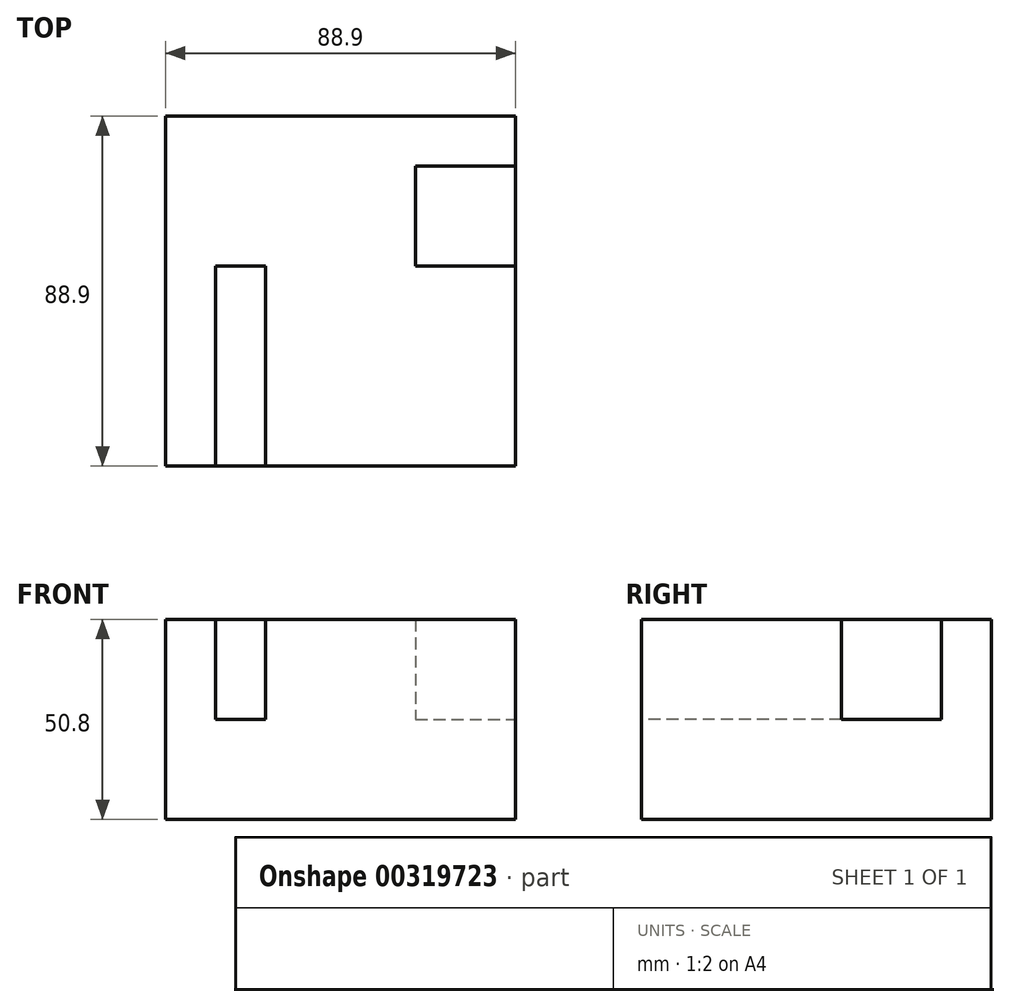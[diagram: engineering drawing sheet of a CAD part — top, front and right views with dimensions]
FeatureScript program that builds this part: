
annotation { "Feature Type Name" : "Feature", "Feature Type Description" : "" }
export const myFeature = defineFeature(function(context is Context, id is Id, definition is map)
    precondition{}
    {
        {
            var Q0;
            Q0=qCreatedBy(makeId("Top.planeOp"),FACE);
            var sketch = newSketch(context, id + "F0", { "sketchPlane" : qUnion([Q0])});
            skLineSegment(sketch, "E0", {"start": v(-35.04, 28.06) * mm, "end": v(-35.04, -60.84) * mm});
            skLineSegment(sketch, "E1", {"start": v(-35.04, -60.84) * mm, "end": v(53.86, -60.84) * mm});
            skLineSegment(sketch, "E2", {"start": v(53.86, -60.84) * mm, "end": v(53.86, 28.06) * mm});
            skLineSegment(sketch, "E3", {"start": v(53.86, 28.06) * mm, "end": v(-35.04, 28.06) * mm});
            skSolve(sketch);
        }
        {
            var Q0;
            Q0=makeQuery(id+"F0.imprint","IMPRINT",FACE,{"disambiguationData":[TD([[makeQuery(id+"F0.imprint","IMPRINT",EDGE,{"derivedFrom":sQuery(id+"F0.wireOp",EDGE,"E0")}),1.0]])]});
            extrude(context, id + "F1", {"entities" : qUnion([Q0]), "depth" : 50.8 * mm});
        }
        {
            var Q0;
            Q0=makeQuery(id+"F1.opExtrude","SWEPT_FACE",FACE,{"disambiguationData":[OSD([sQuery(id+"F0.wireOp",EDGE,"E2")])]});
            var sketch = newSketch(context, id + "F2", { "sketchPlane" : qUnion([Q0])});
            skLineSegment(sketch, "E4", {"start": v(-10.04, 50.8) * mm, "end": v(-10.04, 25.4) * mm});
            skLineSegment(sketch, "E5", {"start": v(-10.04, 25.4) * mm, "end": v(15.36, 25.4) * mm});
            skLineSegment(sketch, "E6", {"start": v(15.36, 25.4) * mm, "end": v(15.36, 50.8) * mm});
            skLineSegment(sketch, "E7", {"start": v(15.36, 50.8) * mm, "end": v(28.06, 50.8) * mm});
            skLineSegment(sketch, "E8", {"start": v(-10.04, 50.8) * mm, "end": v(15.36, 50.8) * mm});
            skSolve(sketch);
        }
        {
            var Q0;
            Q0=makeQuery(id+"F2.imprint","IMPRINT",FACE,{"disambiguationData":[TD([[makeQuery(id+"F2.imprint","IMPRINT",EDGE,{"derivedFrom":sQuery(id+"F2.wireOp",EDGE,"E4")}),1.0]])]});
            extrude(context, id + "F3", {"entities" : qUnion([Q0]), "operationType" : NewBodyOperationType.REMOVE, "oppositeDirection" : true, "depth" : 25.4 * mm});
        }
        {
            var Q0;
            Q0=makeQuery(id+"F1.opExtrude","SWEPT_FACE",FACE,{"disambiguationData":[OSD([sQuery(id+"F0.wireOp",EDGE,"E1")])]});
            var sketch = newSketch(context, id + "F4", { "sketchPlane" : qUnion([Q0])});
            skLineSegment(sketch, "E9", {"start": v(-22.34, 50.8) * mm, "end": v(-22.34, 25.4) * mm});
            skLineSegment(sketch, "E10", {"start": v(-22.34, 25.4) * mm, "end": v(-9.64, 25.4) * mm});
            skLineSegment(sketch, "E11", {"start": v(-9.64, 25.4) * mm, "end": v(-9.64, 50.8) * mm});
            skLineSegment(sketch, "E12", {"start": v(-9.64, 50.8) * mm, "end": v(-22.34, 50.8) * mm});
            skLineSegment(sketch, "E13", {"start": v(-35.04, 50.8) * mm, "end": v(-22.34, 50.8) * mm});
            skSolve(sketch);
        }
        {
            var Q0;
            Q0=makeQuery(id+"F4.imprint","IMPRINT",FACE,{"disambiguationData":[TD([[makeQuery(id+"F4.imprint","IMPRINT",EDGE,{"derivedFrom":sQuery(id+"F4.wireOp",EDGE,"E9")}),1.0]])]});
            extrude(context, id + "F5", {"entities" : qUnion([Q0]), "operationType" : NewBodyOperationType.REMOVE, "oppositeDirection" : true, "depth" : 50.8 * mm});
        }
    });
